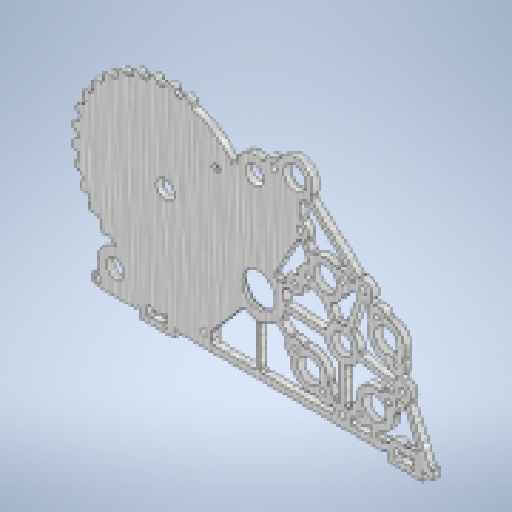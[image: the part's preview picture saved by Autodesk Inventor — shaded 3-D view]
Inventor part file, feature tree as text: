
AUTODESK INVENTOR PART (.ipt)
format: ipt  version: 2023 (Build 270158000, 158)  size: 8,361,984 bytes
history: native  units: mm
features: sketch x48, extrude x45, other x27, projected_geometry x18, fillet x12, hole x7, chamfer x1, pattern_circular x1
ambient origin geometry x8: Origin, YZ Plane, XZ Plane, XY Plane, X Axis, Y Axis, Z Axis, Center Point
bodies: Body1 (feature_tree)
feature tree (159):
  other  "ソリッド1"
  sketch  "スケッチ1"
  extrude  "押し出し1"  Depth=0.95mm
  sketch  "スケッチ3"
  hole  "穴1"  [1 undecoded]
  hole  "穴2"  [1 undecoded]
  hole  "穴3"  [1 undecoded]
  sketch  "スケッチ5"
  sketch  "スケッチ4"
  sketch  "スケッチ6"
  extrude  "押し出し2"  Depth=6.0mm
  extrude  "押し出し4"  Depth=6.0mm
  extrude  "押し出し5"  Depth=12.0mm
  sketch  "スケッチ11"
  extrude  "押し出し6"  Depth=1.0mm
  sketch  "スケッチ12"
  extrude  "押し出し7"  Depth=3.0mm
  hole  "穴4"  [1 undecoded]
  extrude  "押し出し8"  Depth=15.0mm
  extrude  "押し出し9"  Depth=9.0mm
  extrude  "押し出し10"  Depth=5.0mm
  extrude  "押し出し11"  Depth=4.0mm
  extrude  "押し出し12"  Depth=3.0mm
  extrude  "押し出し13"  Depth=16.0mm
  extrude  "押し出し14"  Depth=16.0mm
  extrude  "押し出し15"  Depth=16.0mm
  fillet  "フィレット1"  Radius=16.0mm
  extrude  "押し出し16"  Depth=2.6mm
  hole  "穴5"  [1 undecoded]
  fillet  "フィレット2"  Radius=2.6mm
  extrude  "押し出し17"  Depth=2.6mm
  fillet  "フィレット3"  Radius=2.6mm
  fillet  "フィレット4"  Radius=2.6mm
  sketch  "スケッチ23"
  extrude  "押し出し18"  Depth=2.6mm
  sketch  "スケッチ26"
  extrude  "押し出し19"  Depth=2.6mm
  hole  "穴6"  [1 undecoded]
  extrude  "押し出し20"  Depth=10.5mm
  fillet  "フィレット5"  Radius=10.5mm
  extrude  "押し出し21"  Depth=10.5mm
  extrude  "押し出し22"  Depth=3.0mm
  sketch  "スケッチ30"
  extrude  "押し出し23"  Depth=3.0mm
  extrude  "押し出し24"  Depth=3.0mm
  hole  "穴7"  [1 undecoded]
  extrude  "押し出し25"  Depth=3.0mm
  fillet  "フィレット6"  Radius=3.0mm
  sketch  "スケッチ32"
  sketch  "スケッチ33"
  extrude  "押し出し26"  Depth=3.0mm
  extrude  "押し出し27"  Depth=3.0mm
  extrude  "押し出し28"  Depth=1.0mm
  chamfer  "面取り1"  Distance=1.0mm
  fillet  "フィレット7"  Radius=3.0mm
  extrude  "押し出し29"  Depth=3.0mm
  fillet  "フィレット8"  Radius=3.0mm
  extrude  "押し出し30"  Depth=15.0mm
  sketch  "スケッチ37"
  extrude  "押し出し31"  Depth=3.0mm
  extrude  "押し出し32"  Depth=15.0mm
  extrude  "押し出し33"  Depth=3.0mm
  extrude  "押し出し34"  Depth=3.0mm
  sketch  "スケッチ40"
  fillet  "フィレット9"  Radius=3.0mm
  sketch  "スケッチ41"
  extrude  "押し出し35"  Depth=3.0mm
  extrude  "押し出し36"  Depth=3.0mm
  sketch  "スケッチ42"
  extrude  "押し出し37"  Depth=3.0mm TaperAngle=0.0deg
  extrude  "押し出し38"  Depth=6.618835mm
  extrude  "押し出し39"  Depth=50.0mm
  extrude  "押し出し40"  Depth=8.0mm
  sketch  "スケッチ45"
  extrude  "押し出し41"  Depth=4.0mm
  extrude  "押し出し42"  Depth=4.0mm
  extrude  "押し出し43"  Depth=4.0mm
  extrude  "押し出し44"  Depth=3.0mm TaperAngle=0.0deg
  extrude  "押し出し45"  Depth=8.0mm
  fillet  "フィレット10"  Radius=10.0mm
  fillet  "フィレット11"  Radius=8.0mm
  fillet  "フィレット12"  Radius=4.0mm
  sketch  "スケッチ48"
  extrude  "押し出し46"  Depth=1.396263mm
  pattern_circular  "円形状パターン1"  [2 undecoded]
  sketch  "スケッチ2"
  projected_geometry  "投影ループ1"
  sketch  "スケッチ7"
  sketch  "スケッチ8"
  sketch  "スケッチ10"
  sketch  "スケッチ13"
  sketch  "スケッチ14"
  sketch  "スケッチ15"
  sketch  "スケッチ16"
  sketch  "スケッチ17"
  sketch  "スケッチ18"
  sketch  "スケッチ19"
  sketch  "スケッチ20"
  sketch  "スケッチ21"
  sketch  "スケッチ22"
  sketch  "スケッチ24"
  sketch  "スケッチ25"
  projected_geometry  "投影ループ2"
  sketch  "スケッチ27"
  projected_geometry  "投影ループ3"
  sketch  "スケッチ28"
  projected_geometry  "投影ループ4"
  sketch  "スケッチ29"
  sketch  "スケッチ31"
  projected_geometry  "投影ループ5"
  sketch  "スケッチ34"
  projected_geometry  "投影ループ6"
  sketch  "スケッチ35"
  sketch  "スケッチ36"
  projected_geometry  "投影ループ7"
  projected_geometry  "投影ループ8"
  sketch  "スケッチ38"
  projected_geometry  "投影ループ9"
  sketch  "スケッチ39"
  projected_geometry  "投影ループ10"
  projected_geometry  "投影ループ11"
  projected_geometry  "投影ループ12"
  projected_geometry  "投影ループ13"
  projected_geometry  "投影ループ14"
  sketch  "スケッチ43"
  projected_geometry  "投影ループ15"
  sketch  "スケッチ44"
  projected_geometry  "投影ループ16"
  sketch  "スケッチ46"
  projected_geometry  "投影ループ17"
  sketch  "スケッチ47"
  projected_geometry  "投影ループ18"
  sketch  "スケッチ49"
  other  "断面エッジを投影1"
  other  "断面エッジを投影2"
  other  "断面エッジを投影3"
  other  "断面エッジを投影4"
  other  "断面エッジを投影6"
  other  "断面エッジを投影7"
  other  "断面エッジを投影8"
  other  "断面エッジを投影9"
  other  "断面エッジを投影10"
  other  "断面エッジを投影11"
  other  "断面エッジを投影12"
  other  "断面エッジを投影13"
  other  "断面エッジを投影14"
  other  "断面エッジを投影15"
  other  "断面エッジを投影16"
  other  "断面エッジを投影17"
  other  "断面エッジを投影18"
  other  "断面エッジを投影19"
  other  "断面エッジを投影20"
  other  "断面エッジを投影21"
  other  "断面エッジを投影22"
  other  "断面エッジを投影23"
  other  "断面エッジを投影24"
  other  "断面エッジを投影25"
  other  "断面エッジを投影26"
  other  "断面エッジを投影27"
note: 9 required parameter values undecoded (feature->parameter linkage not recoverable at this tier; creation-order binding heuristic only, values carry confidence <= 0.55)
